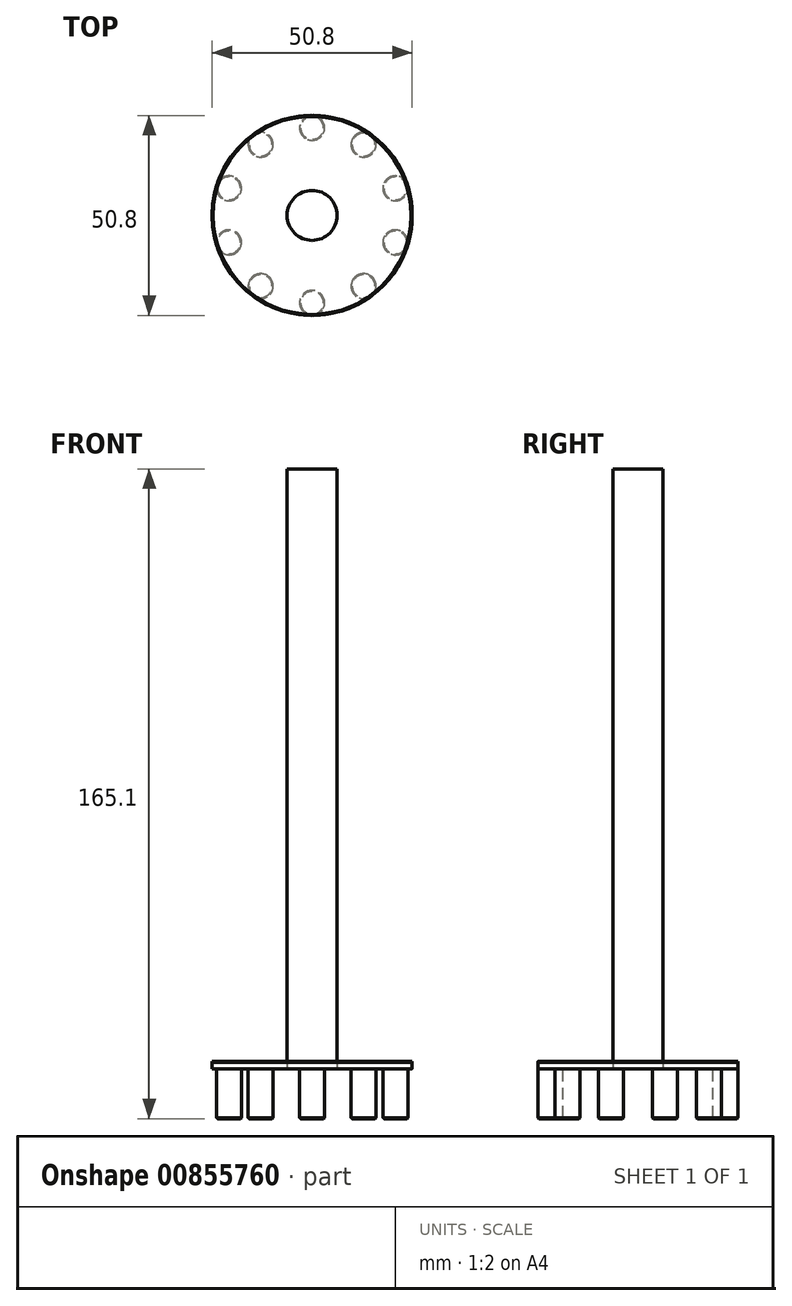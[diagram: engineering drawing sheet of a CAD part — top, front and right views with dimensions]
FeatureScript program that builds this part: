
annotation { "Feature Type Name" : "Feature", "Feature Type Description" : "" }
export const myFeature = defineFeature(function(context is Context, id is Id, definition is map)
    precondition{}
    {
        {
            var Q0;
            Q0=qCreatedBy(makeId("Top.planeOp"),FACE);
            var sketch = newSketch(context, id + "F0", { "sketchPlane" : qUnion([Q0])});
            skCircle(sketch, "E0", {"center": v(0, 0) * mm, "radius": 25.4 * mm});
            skSolve(sketch);
        }
        {
            var Q0;
            Q0=makeQuery(id+"F0.imprint","IMPRINT",FACE,{"disambiguationData":[TD([[makeQuery(id+"F0.imprint","IMPRINT",EDGE,{"derivedFrom":sQuery(id+"F0.wireOp",EDGE,"E0")}),1.0]])]});
            var Q1;
            Q1=sQuery(id+"F0.wireOp",EDGE,"E0");
            extrude(context, id + "F1", {"entities" : qUnion([Q0]), "surfaceEntities" : qUnion([Q1]), "depth" : 1.9 * mm, "offsetDistance" : 25.4 * mm});
        }
        {
            var Q0;
            Q0=qCreatedBy(makeId("Top.planeOp"),FACE);
            var sketch = newSketch(context, id + "F2", { "sketchPlane" : qUnion([Q0])});
            skCircle(sketch, "E1", {"center": v(0, 0) * mm, "radius": 6.35 * mm});
            skSolve(sketch);
        }
        {
            var Q0;
            Q0 = qSketchRegion(id + "F2", true);
            extrude(context, id + "F3", {"entities" : qUnion([Q0]), "depth" : 152.4 * mm, "offsetDistance" : 25.4 * mm});
        }
        {
            var Q0;
            Q0=makeQuery(id+"F1.opExtrude","CAP_FACE",FACE,{"disambiguationData":[OSD([sQuery(id+"F0.wireOp",EDGE,"E0")])],"isStart":true});
            var sketch = newSketch(context, id + "F4", { "sketchPlane" : qUnion([Q0])});
            skCircle(sketch, "E2", {"center": v(0, 22.23) * mm, "radius": 3.18 * mm});
            skSolve(sketch);
        }
        {
            var Q0;
            Q0 = qSketchRegion(id + "F4", true);
            extrude(context, id + "F5", {"entities" : qUnion([Q0]), "operationType" : NewBodyOperationType.ADD, "depth" : 12.7 * mm, "offsetDistance" : 25.4 * mm});
        }
        {
            var Q0;
            Q0=makeQuery(id+"F1.opExtrude","SWEPT_BODY",BODY,{"disambiguationData":[OSD([sQuery(id+"F0.wireOp",EDGE,"E0")])]});
            var Q1;
            Q1=makeQuery(id+"F3.opExtrude","SWEPT_FACE",FACE,{"disambiguationData":[OSD([sQuery(id+"F2.wireOp",EDGE,"E1")])]});
            circularPattern(context, id + "F6", {"entities" : qUnion([Q0]), "axis" : qUnion([Q1]), "angle" : 360 * degree, "instanceCount" : 10, "equalSpace" : true});
        }
        {
            var Q0;
            Q0=makeQuery(id+"F6.opPattern","COPY",EDGE,{"derivedFrom":makeQuery(id+"F1.opExtrude","CAP_EDGE",EDGE,{"disambiguationData":[OSD([sQuery(id+"F0.wireOp",EDGE,"E0")])],"isStart":false}),"instanceName":"6"});
            var Q1;
            Q1=makeQuery(id+"F6.opPattern","COPY",EDGE,{"derivedFrom":makeQuery(id+"F5.opExtrude","CAP_EDGE",EDGE,{"disambiguationData":[OSD([sQuery(id+"F4.wireOp",EDGE,"E2")])],"isStart":false}),"instanceName":"13"});
            var Q2;
            Q2=makeQuery(id+"F5.opExtrude","CAP_EDGE",EDGE,{"disambiguationData":[OSD([sQuery(id+"F4.wireOp",EDGE,"E2")])],"isStart":false});
            var Q3;
            Q3=makeQuery(id+"F6.opPattern","COPY",EDGE,{"derivedFrom":makeQuery(id+"F5.opExtrude","CAP_EDGE",EDGE,{"disambiguationData":[OSD([sQuery(id+"F4.wireOp",EDGE,"E2")])],"isStart":false}),"instanceName":"1"});
            var Q4;
            Q4=makeQuery(id+"F6.opPattern","COPY",EDGE,{"derivedFrom":makeQuery(id+"F5.opExtrude","CAP_EDGE",EDGE,{"disambiguationData":[OSD([sQuery(id+"F4.wireOp",EDGE,"E2")])],"isStart":false}),"instanceName":"12"});
            var Q5;
            Q5=makeQuery(id+"F6.opPattern","COPY",EDGE,{"derivedFrom":makeQuery(id+"F5.opExtrude","CAP_EDGE",EDGE,{"disambiguationData":[OSD([sQuery(id+"F4.wireOp",EDGE,"E2")])],"isStart":false}),"instanceName":"10"});
            var Q6;
            Q6=makeQuery(id+"F6.opPattern","COPY",EDGE,{"derivedFrom":makeQuery(id+"F5.opExtrude","CAP_EDGE",EDGE,{"disambiguationData":[OSD([sQuery(id+"F4.wireOp",EDGE,"E2")])],"isStart":false}),"instanceName":"11"});
            var Q7;
            Q7=makeQuery(id+"F6.opPattern","COPY",EDGE,{"derivedFrom":makeQuery(id+"F5.opExtrude","CAP_EDGE",EDGE,{"disambiguationData":[OSD([sQuery(id+"F4.wireOp",EDGE,"E2")])],"isStart":false}),"instanceName":"3"});
            var Q8;
            Q8=makeQuery(id+"F6.opPattern","COPY",EDGE,{"derivedFrom":makeQuery(id+"F5.opExtrude","CAP_EDGE",EDGE,{"disambiguationData":[OSD([sQuery(id+"F4.wireOp",EDGE,"E2")])],"isStart":false}),"instanceName":"4"});
            var Q9;
            Q9=makeQuery(id+"F6.opPattern","COPY",EDGE,{"derivedFrom":makeQuery(id+"F5.opExtrude","CAP_EDGE",EDGE,{"disambiguationData":[OSD([sQuery(id+"F4.wireOp",EDGE,"E2")])],"isStart":false}),"instanceName":"5"});
            var Q10;
            Q10=makeQuery(id+"F6.opPattern","COPY",EDGE,{"derivedFrom":makeQuery(id+"F5.opExtrude","CAP_EDGE",EDGE,{"disambiguationData":[OSD([sQuery(id+"F4.wireOp",EDGE,"E2")])],"isStart":false}),"instanceName":"6"});
            var Q11;
            Q11=makeQuery(id+"F6.opPattern","COPY",EDGE,{"derivedFrom":makeQuery(id+"F5.opExtrude","CAP_EDGE",EDGE,{"disambiguationData":[OSD([sQuery(id+"F4.wireOp",EDGE,"E2")])],"isStart":false}),"instanceName":"7"});
            var Q12;
            Q12=makeQuery(id+"F6.opPattern","COPY",EDGE,{"derivedFrom":makeQuery(id+"F5.opExtrude","CAP_EDGE",EDGE,{"disambiguationData":[OSD([sQuery(id+"F4.wireOp",EDGE,"E2")])],"isStart":false}),"instanceName":"2"});
            var Q13;
            Q13=makeQuery(id+"F6.opPattern","COPY",EDGE,{"derivedFrom":makeQuery(id+"F5.opExtrude","CAP_EDGE",EDGE,{"disambiguationData":[OSD([sQuery(id+"F4.wireOp",EDGE,"E2")])],"isStart":false}),"instanceName":"8"});
            var Q14;
            Q14=makeQuery(id+"F6.opPattern","COPY",EDGE,{"derivedFrom":makeQuery(id+"F5.opExtrude","CAP_EDGE",EDGE,{"disambiguationData":[OSD([sQuery(id+"F4.wireOp",EDGE,"E2")])],"isStart":false}),"instanceName":"9"});
            chamfer(context, id + "F7", {"entities" : qUnion([Q0, Q1, Q2, Q3, Q4, Q5, Q6, Q7, Q8, Q9, Q10, Q11, Q12, Q13, Q14]), "width" : 0.25 * mm, "tangentPropagation" : true});
        }
    });
